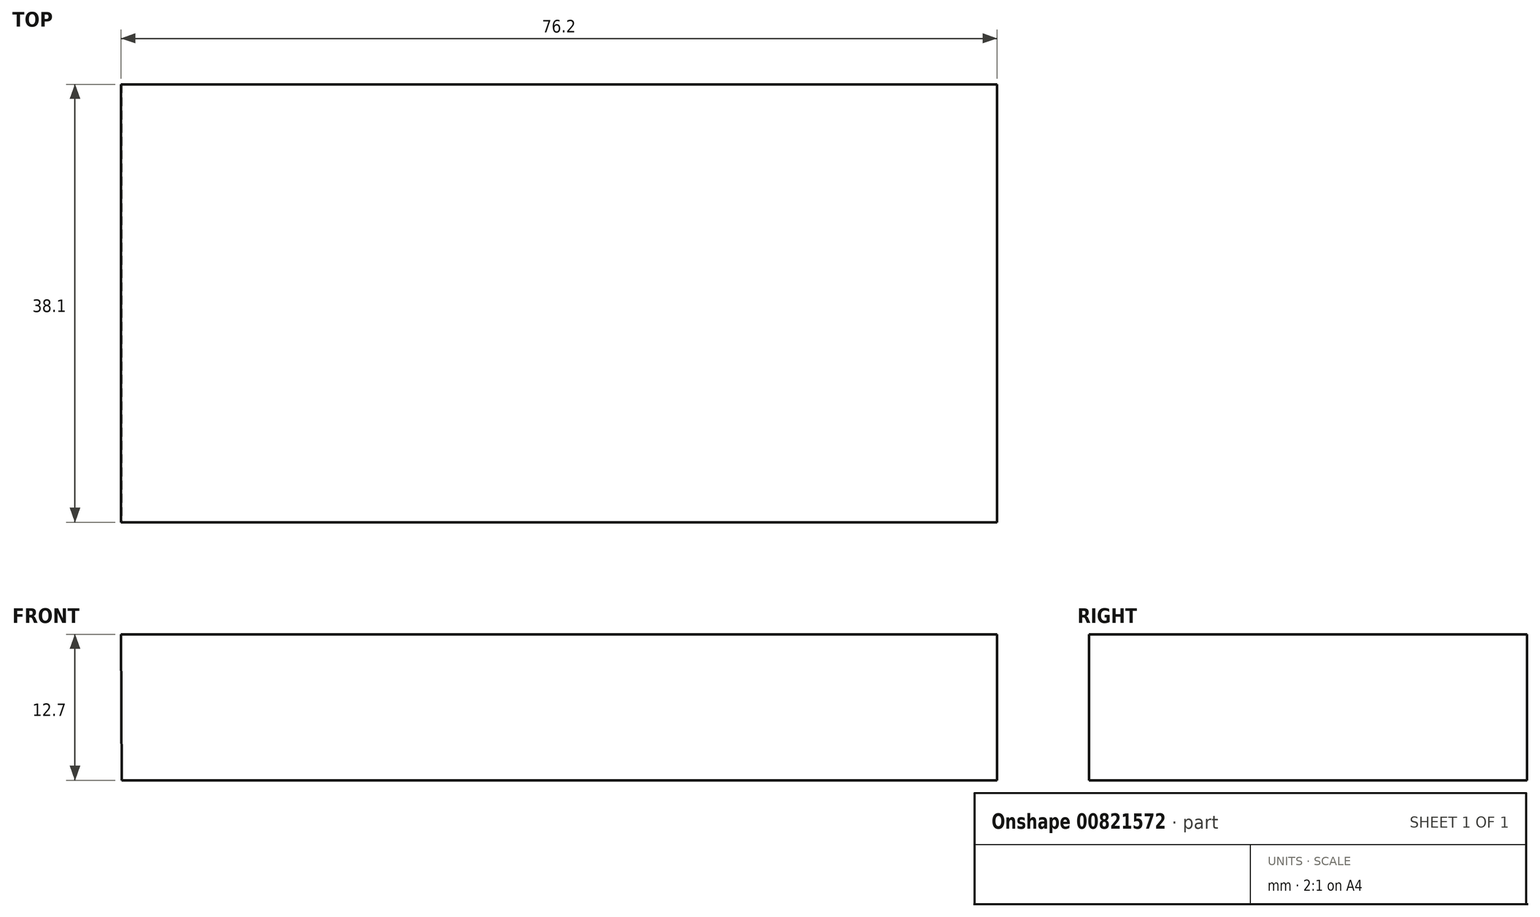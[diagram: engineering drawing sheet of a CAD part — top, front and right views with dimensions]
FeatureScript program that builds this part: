
annotation { "Feature Type Name" : "Feature", "Feature Type Description" : "" }
export const myFeature = defineFeature(function(context is Context, id is Id, definition is map)
    precondition{}
    {
        {
            var Q0;
            Q0=qCreatedBy(makeId("Front.planeOp"),FACE);
            var sketch = newSketch(context, id + "F0", { "sketchPlane" : qUnion([Q0])});
            skLineSegment(sketch, "E0", {"start": v(0, 0) * mm, "end": v(-50.8, 0) * mm});
            skLineSegment(sketch, "E1", {"start": v(-0.06, 0) * mm, "end": v(25.34, 0) * mm});
            skLineSegment(sketch, "E2", {"start": v(25.34, 0) * mm, "end": v(25.34, 12.7) * mm});
            skLineSegment(sketch, "E3", {"start": v(25.34, 12.7) * mm, "end": v(-50.86, 12.7) * mm});
            skLineSegment(sketch, "E4", {"start": v(-50.86, 12.7) * mm, "end": v(-50.8, 0) * mm});
            skSolve(sketch);
        }
        {
            var Q0;
            {var subQ2=sQuery(id+"F0.wireOp",EDGE,"E0");Q0=makeQuery(id+"F0.imprint","IMPRINT",FACE,{"disambiguationData":[TD([[makeQuery(id+"F0.imprint","IMPRINT",EDGE,{"derivedFrom":subQ2}),-1.0]])]});}
            extrude(context, id + "F1", {"entities" : qUnion([Q0]), "oppositeDirection" : true, "depth" : 38.1 * mm, "offsetDistance" : 25.4 * mm});
        }
    });
